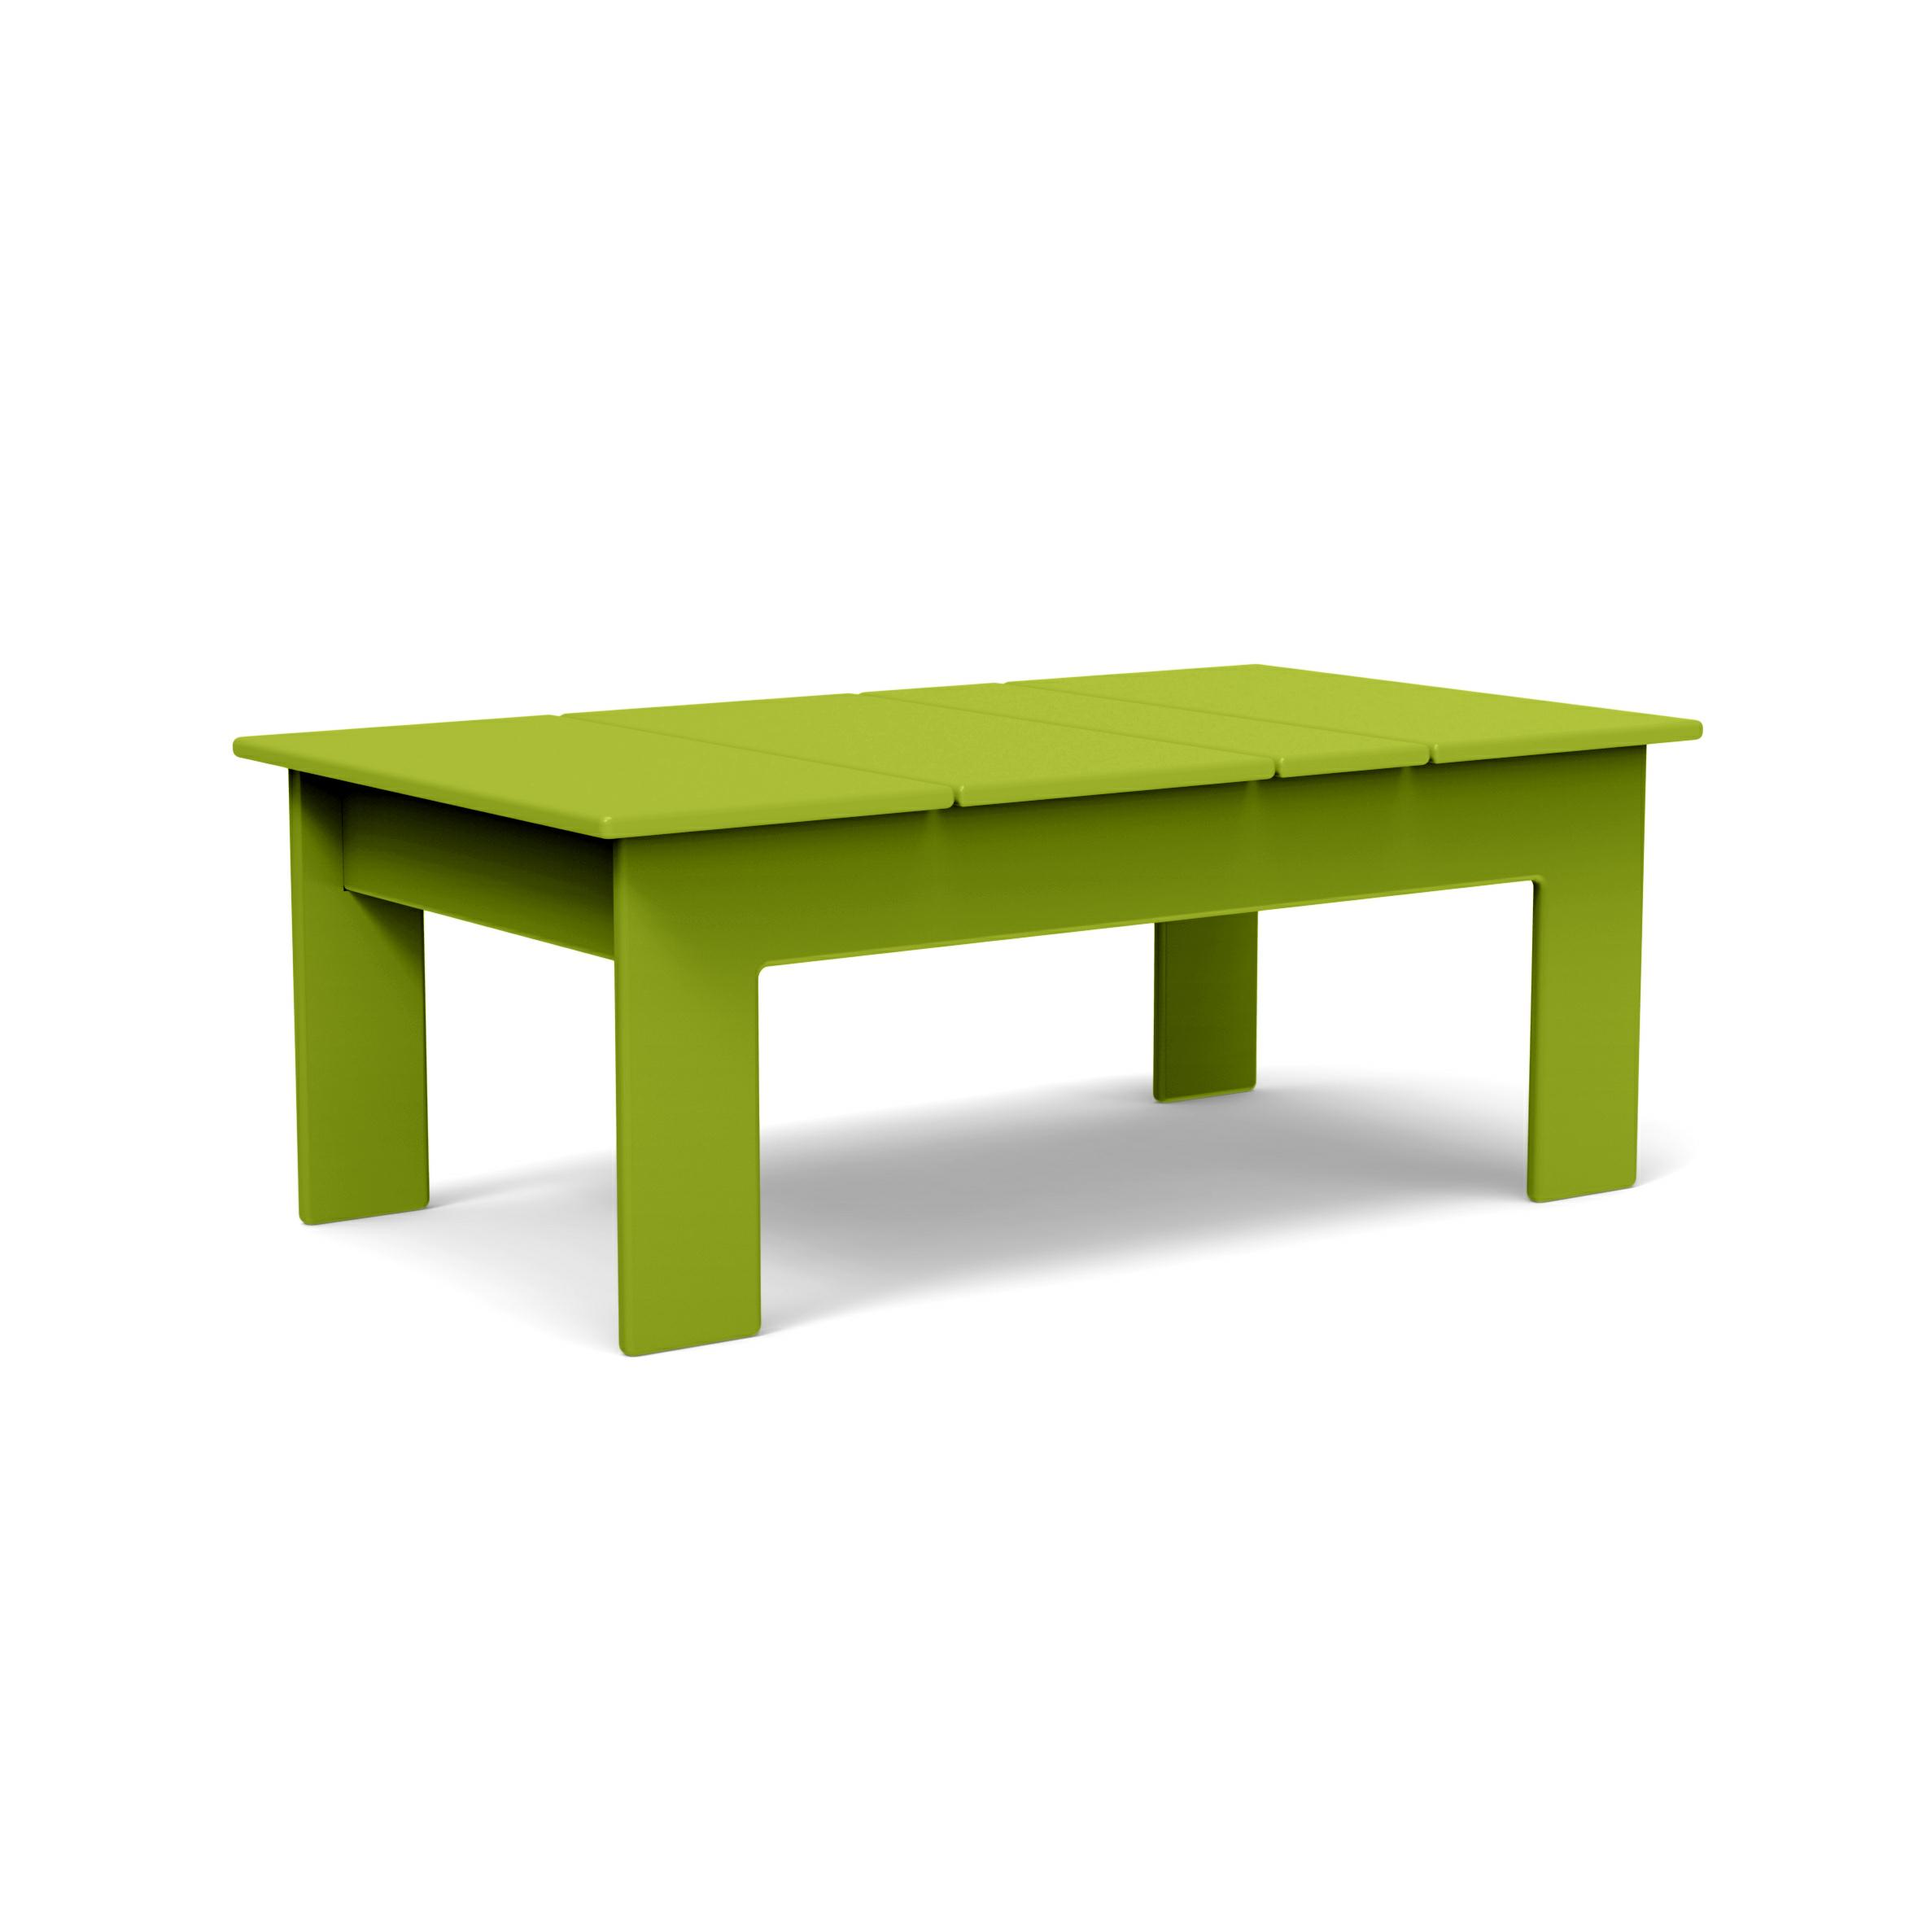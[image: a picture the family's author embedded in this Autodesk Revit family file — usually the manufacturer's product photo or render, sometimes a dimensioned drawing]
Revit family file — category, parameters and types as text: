
# Revit family: Lollygagger Cocktail Table Rectangle
name_source: partatom
category: Furniture
revit_build: Autodesk Revit 2016 (Build: 20150220_1215(x64)
units: mm (PartAtom-declared; Revit-internal decimal feet)

## family parameters
Always vertical = Yes
Cut with Voids When Loaded = No
OmniClass Number = 23.40.20.00
OmniClass Title = General Furniture and Specialties
Room Calculation Point = No
Shared = No
Work Plane-Based = No

## types (11) — shared parameters
Apron = 3 5/16"
Height Top = 12 1/16"
Lenght = 32"
Manufacturer = Loll
Thick = 1/2"
Type Image = lollygagger_cocktail_rect_green.jpg
URL = https://lolldesigns.com
Width = 18"
with Leg = 3 1/2"

## per-type parameters (varying)
| type | Finish Material |
| Loll-Black | Loll-Black |
| Loll-Sunset | Loll-Sunset |
| Loll-Chocolate | Loll-Chocolate |
| Loll-Sky | Loll-Sky |
| Loll-Apple | Loll-Apple |
| Loll-Leaf | Loll-Evergreen |
| Loll-Evergreen | Loll-Leaf |
| Loll-Charcoal | Loll-Charcoal |
| Loll-Sand | Loll-Sand |
| Loll-Navy Blue | Loll-Navy Blue |
| Loll-White | Loll-White |

## geometry (parser evidence)
native form markers: Sweep x1
no freeform markers — native parametric forms only
